# Revit family: AVS 315
name_source: partatom
category: Mechanical Equipment
units: mm (PartAtom-declared; Revit-internal decimal feet)

## family parameters
Always vertical = No
Classification = None
Cut with Voids When Loaded = No
Maintain Annotation Orientation = No
OmniClass Number = 23.75.35.17.11
OmniClass Title = Fans for Air Ductwork
Part Type = Breaks Into
Room Calculation Point = No
Round Connector Dimension = Use Diameter
Shared = No
Work Plane-Based = No

## types (1)
- Aventa Silent AVS315
    Apparent Power = 320 VA
    Current = 1 A
    D = 315 mm  [stored 1.03346 ft]
    D1 = 432 mm  [stored 1.41732 ft]
    Dd12 = 1 mm  [stored 0.00328084 ft]
    Dd13 = 2 mm  [stored 0.00656168 ft]
    Dd14 = 6 mm  [stored 0.019685 ft]
    Dd16 = 55 mm  [stored 0.180446 ft]
    Dd22 = 5 mm  [stored 0.0164042 ft]
    Dd23 = 6 mm  [stored 0.019685 ft]
    Dd24 = 30 mm  [stored 0.0984252 ft]
    Dd26 = 52 mm
    Default Elevation = 0 mm  [stored 0 ft]
    Description = Inline mixed-flow fan suitable for domestic and light commercial facilities
    Distribution Box Material = Distribution Box Dark Grey
    Duct Connection Size = 315 mm  [stored 1.03346 ft]
    ElBoxH = 53 mm  [stored 0.173885 ft]
    ElBoxL = 104 mm
    ElBoxR = 15 mm  [stored 0.0492126 ft]
    ElBoxW = 104 mm
    Family Version = 1.0
    Fan Material = Metal Black
    Hanger Material = Metal Zinc
    HangerBaseH = 219 mm  [stored 0.718504 ft]
    HangerExtraL = No
    HangerH = 219 mm  [stored 0.718504 ft]
    HangerL = 478 mm  [stored 1.56824 ft]
    HangerL1 = 396 mm  [stored 1.29921 ft]
    HangerW = 200 mm  [stored 0.656168 ft]
    L = 780 mm  [stored 2.55906 ft]
    L1 = 32 mm  [stored 0.104987 ft]
    L11 = 195 mm  [stored 0.639764 ft]
    L12 = 8 mm  [stored 0.0262467 ft]
    L13 = 8 mm  [stored 0.0262467 ft]
    L14 = 10 mm  [stored 0.0328084 ft]
    L15 = 153 mm  [stored 0.501969 ft]
    L16 = 6 mm  [stored 0.019685 ft]
    L17 = 10 mm  [stored 0.0328084 ft]
    L2 = 32 mm  [stored 0.104987 ft]
    L21 = 218 mm  [stored 0.715223 ft]
    L22 = 8 mm  [stored 0.0262467 ft]
    L23 = 13 mm
    L24 = 27 mm  [stored 0.0885827 ft]
    L25 = 154 mm
    L26 = 6 mm  [stored 0.019685 ft]
    L27 = 10 mm  [stored 0.0328084 ft]
    Load Classification = HVAC
    Maintenance Zone Height = 600 mm  [stored 1.9685 ft]
    Maintenance Zone Length = 600 mm  [stored 1.9685 ft]
    Maintenance Zone Length Calc = 780 mm  [stored 2.55906 ft]
    Maintenance Zone Material = Maintenance Zone
    Maintenance Zone Width = 600 mm  [stored 1.9685 ft]
    Manufacturer = Airflow
    Maximum Air Flow = 2050 m³/h
    Model = Aventa Silent AVS315
    Noise Level at 3 m (dBa) = 40
    Number of Poles = 1
    Power = 320 W
    Power Factor = 1
    Protection rating = IPX4
    R1 = 216 mm  [stored 0.708661 ft]
    RPM (min-1) = 2430
    Transported Air Temperature (°C) = -25...+60
    Type Comments = Inline fan single speed up to 2050m3/h
    URL = https://www.airflow.com
    Voltage = 230 V
    Weight = 25.00 kg

note: [stored X ft] marks values corroborated as IEEE doubles in the binary element streams (Revit-internal decimal feet)

## geometry (parser evidence)
native form markers: Sweep x11
no freeform markers — native parametric forms only
